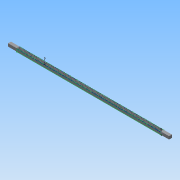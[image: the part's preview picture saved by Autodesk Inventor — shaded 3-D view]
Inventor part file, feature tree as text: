
AUTODESK INVENTOR PART (.ipt)
format: ipt  version: 2015 (Build 190159000, 159)  size: 1,920,000 bytes
history: native  units: in
note: dims shown in document units (in); Inventor stores cm internally (conversion verified against a paired STEP export)
features: sketch x5, projected_geometry x3, other x2, extrude x2, imported_body x1
ambient origin geometry x8: Origin, YZ Plane, XZ Plane, XY Plane, X Axis, Y Axis, Z Axis, Center Point
bodies: Body1 (feature_tree)
feature tree (13):
  parser-record x1  (decoder bookkeeping rows leaked as tree rows — omitted from the tree; the rows remain in map.json)
  other  "KKS10-10-51"
  sketch  "Sketch1"  dims[d2=0.0394in d3=0.0394in]
  sketch  "Sketch2"  dims[d10=19.685in d11=0.5906in]
  extrude  "Extrusion2"  Depth=0.0394in
  extrude  "Extrusion3"  Depth=19.685in
  sketch  "Sketch6"  dims[d15=1.1811in d16=0.3937in d17=1.1811in d18=0.3937in d19=0.0in]
  imported_body  "Base1"
  projected_geometry  "Projected Loop1"
  projected_geometry  "Projected Loop2"
  sketch  "Sketch4"  dims[d12=0.3937in d13=0.0in]
  sketch  "Sketch5"  dims[d14=0.3937in]
  projected_geometry  "Projected Loop4"
